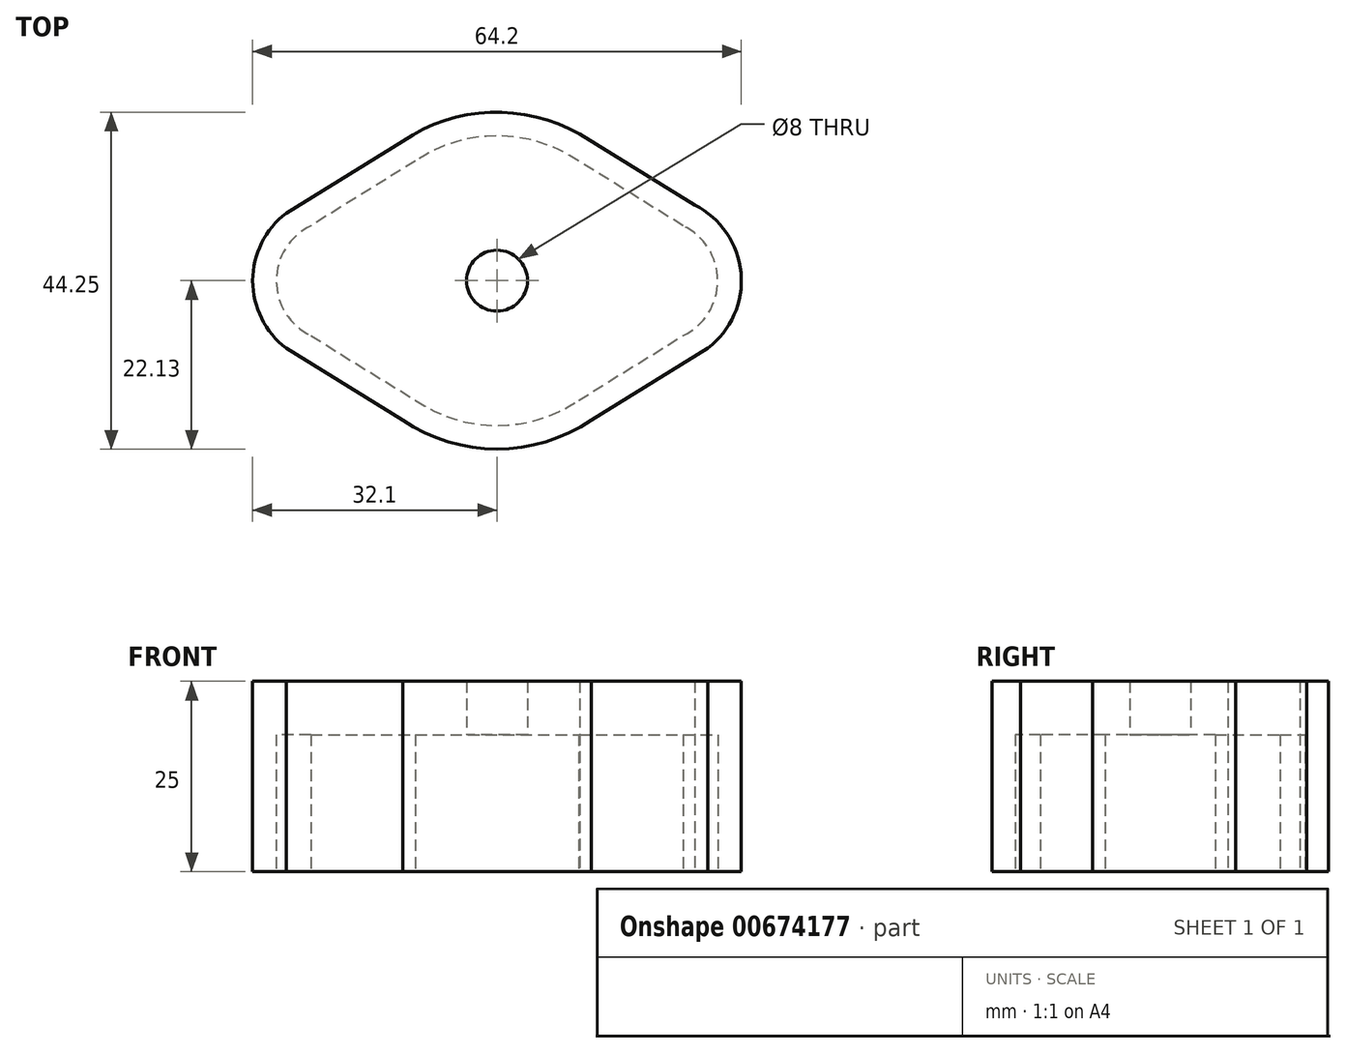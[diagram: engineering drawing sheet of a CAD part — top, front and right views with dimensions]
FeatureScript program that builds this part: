
annotation { "Feature Type Name" : "Feature", "Feature Type Description" : "" }
export const myFeature = defineFeature(function(context is Context, id is Id, definition is map)
    precondition{}
    {
        {
            var Q0;
            Q0=qCreatedBy(makeId("Top.planeOp"),FACE);
            var sketch = newSketch(context, id + "F0", { "sketchPlane" : qUnion([Q0])});
            skPoint(sketch, "E0.middle", {"position": v(0, 0) * mm});
            skArc(sketch, "E1", {"start": v(-12.4, -18.33) * mm, "mid": v(0, -22.12) * mm, "end": v(12.4, -18.33) * mm});
            skLineSegment(sketch, "E2", {"start": v(-27.68, 8.86) * mm, "end": v(-10.88, 19.27) * mm});
            skLineSegment(sketch, "E3", {"start": v(10.88, 19.27) * mm, "end": v(27.68, 8.86) * mm});
            skLineSegment(sketch, "E4", {"start": v(27.68, -8.86) * mm, "end": v(10.88, -19.27) * mm});
            skLineSegment(sketch, "E5", {"start": v(-10.88, -19.27) * mm, "end": v(-27.68, -8.86) * mm});
            skPoint(sketch, "E6.orphan", {"position": v(0, 26) * mm});
            skPoint(sketch, "E7.orphan", {"position": v(0, -26) * mm});
            skArc(sketch, "E8.trimOffspring", {"start": v(12.4, 18.33) * mm, "mid": v(0, 22.12) * mm, "end": v(-12.4, 18.33) * mm});
            skPoint(sketch, "E9.startSnap0", {"position": v(-21, -13) * mm});
            skArc(sketch, "E10", {"start": v(-25.95, 9.93) * mm, "mid": v(-32.1, 0) * mm, "end": v(-25.95, -9.93) * mm});
            skPoint(sketch, "E11.orphan", {"position": v(-42, 0) * mm});
            skArc(sketch, "E12.MirrorC", {"start": v(25.95, 9.93) * mm, "mid": v(32.1, 0) * mm, "end": v(25.95, -9.93) * mm});
            skPoint(sketch, "E13.orphan", {"position": v(42, 0) * mm});
            skPoint(sketch, "E14.start.orphan", {"position": v(-21, -26) * mm});
            skPoint(sketch, "E15.orphan", {"position": v(-42, 26) * mm});
            skPoint(sketch, "E16.orphan", {"position": v(42, 26) * mm});
            skPoint(sketch, "E17.orphan", {"position": v(-42, -26) * mm});
            skPoint(sketch, "E0.top.start.orphan", {"position": v(42, -26) * mm});
            skSolve(sketch);
        }
        {
            var Q0;
            {var subQ0=sQuery(id+"F0.wireOp",EDGE,"E5");var subQ1=sQuery(id+"F0.wireOp",EDGE,"E1");var subQ2=makeQuery(id+"F0.imprint","INTERSECT",VERTEX,{"disambiguationData":[OD(0.0)],"derivedFrom":[subQ1,subQ0]});Q0=makeQuery(id+"F0.imprint","IMPRINT",FACE,{"disambiguationData":[TD([[makeQuery(id+"F0.imprint","IMPRINT",EDGE,{"disambiguationData":[TD([[subQ2,-1.0]])],"derivedFrom":subQ1}),1.0]])]});}
            var Q1;
            {var subQ0=sQuery(id+"F0.wireOp",EDGE,"E4");var subQ1=sQuery(id+"F0.wireOp",EDGE,"E1");var subQ2=makeQuery(id+"F0.imprint","INTERSECT",VERTEX,{"disambiguationData":[OD(0.0)],"derivedFrom":[subQ1,subQ0]});Q1=makeQuery(id+"F0.imprint","IMPRINT",FACE,{"disambiguationData":[TD([[makeQuery(id+"F0.imprint","IMPRINT",EDGE,{"disambiguationData":[TD([[subQ2,1.0]])],"derivedFrom":subQ1}),1.0]])]});}
            var Q2;
            {var subQ0=sQuery(id+"F0.wireOp",EDGE,"E10");var subQ1=sQuery(id+"F0.wireOp",EDGE,"E2");var subQ2=makeQuery(id+"F0.imprint","INTERSECT",VERTEX,{"disambiguationData":[OD(0.0)],"derivedFrom":[subQ1,subQ0]});Q2=makeQuery(id+"F0.imprint","IMPRINT",FACE,{"disambiguationData":[TD([[makeQuery(id+"F0.imprint","IMPRINT",EDGE,{"disambiguationData":[TD([[subQ2,-1.0]])],"derivedFrom":subQ1}),1.0]])]});}
            var Q3;
            {var subQ0=sQuery(id+"F0.wireOp",EDGE,"E8.trimOffspring");var subQ1=sQuery(id+"F0.wireOp",EDGE,"E2");var subQ2=makeQuery(id+"F0.imprint","INTERSECT",VERTEX,{"disambiguationData":[OD(0.0)],"derivedFrom":[subQ1,subQ0]});Q3=makeQuery(id+"F0.imprint","IMPRINT",FACE,{"disambiguationData":[TD([[makeQuery(id+"F0.imprint","IMPRINT",EDGE,{"disambiguationData":[TD([[subQ2,1.0]])],"derivedFrom":subQ1}),1.0]])]});}
            var Q4;
            {var subQ0=sQuery(id+"F0.wireOp",EDGE,"E8.trimOffspring");var subQ1=sQuery(id+"F0.wireOp",EDGE,"E3");var subQ2=makeQuery(id+"F0.imprint","INTERSECT",VERTEX,{"disambiguationData":[OD(0.0)],"derivedFrom":[subQ1,subQ0]});Q4=makeQuery(id+"F0.imprint","IMPRINT",FACE,{"disambiguationData":[TD([[makeQuery(id+"F0.imprint","IMPRINT",EDGE,{"disambiguationData":[TD([[subQ2,-1.0]])],"derivedFrom":subQ1}),1.0]])]});}
            var Q5;
            {var subQ0=sQuery(id+"F0.wireOp",EDGE,"E12.MirrorC");var subQ1=sQuery(id+"F0.wireOp",EDGE,"E3");var subQ2=makeQuery(id+"F0.imprint","INTERSECT",VERTEX,{"disambiguationData":[OD(0.0)],"derivedFrom":[subQ1,subQ0]});Q5=makeQuery(id+"F0.imprint","IMPRINT",FACE,{"disambiguationData":[TD([[makeQuery(id+"F0.imprint","IMPRINT",EDGE,{"disambiguationData":[TD([[subQ2,1.0]])],"derivedFrom":subQ1}),1.0]])]});}
            var Q6;
            {var subQ0=sQuery(id+"F0.wireOp",EDGE,"E12.MirrorC");var subQ1=sQuery(id+"F0.wireOp",EDGE,"E4");var subQ2=makeQuery(id+"F0.imprint","INTERSECT",VERTEX,{"disambiguationData":[OD(0.0)],"derivedFrom":[subQ1,subQ0]});Q6=makeQuery(id+"F0.imprint","IMPRINT",FACE,{"disambiguationData":[TD([[makeQuery(id+"F0.imprint","IMPRINT",EDGE,{"disambiguationData":[TD([[subQ2,-1.0]])],"derivedFrom":subQ1}),1.0]])]});}
            var Q7;
            {var subQ0=sQuery(id+"F0.wireOp",EDGE,"E10");var subQ1=sQuery(id+"F0.wireOp",EDGE,"E5");var subQ2=makeQuery(id+"F0.imprint","INTERSECT",VERTEX,{"disambiguationData":[OD(0.0)],"derivedFrom":[subQ1,subQ0]});Q7=makeQuery(id+"F0.imprint","IMPRINT",FACE,{"disambiguationData":[TD([[makeQuery(id+"F0.imprint","IMPRINT",EDGE,{"disambiguationData":[TD([[subQ2,1.0]])],"derivedFrom":subQ1}),1.0]])]});}
            var Q8;
            {var subQ0=sQuery(id+"F0.wireOp",EDGE,"E4");var subQ1=sQuery(id+"F0.wireOp",EDGE,"E1");var subQ3=makeQuery(id+"F0.imprint","INTERSECT",VERTEX,{"disambiguationData":[OD(1.0)],"derivedFrom":[subQ1,subQ0]});Q8=makeQuery(id+"F0.imprint","IMPRINT",FACE,{"disambiguationData":[TD([[makeQuery(id+"F0.imprint","IMPRINT",EDGE,{"disambiguationData":[TD([[subQ3,1.0]])],"derivedFrom":subQ1}),1.0]])]});}
            extrude(context, id + "F1", {"entities" : qUnion([Q0, Q1, Q2, Q3, Q4, Q5, Q6, Q7, Q8]), "depth" : 25 * mm, "offsetDistance" : 25 * mm});
        }
        {
            var Q0;
            Q0=qCreatedBy(makeId("Top.planeOp"),FACE);
            var sketch = newSketch(context, id + "F2", { "sketchPlane" : qUnion([Q0])});
            skLineSegment(sketch, "E18.0", {"start": v(-24.45, -7.22) * mm, "end": v(-10.7, -15.72) * mm});
            skArc(sketch, "E18.1", {"start": v(-24.45, 7.22) * mm, "mid": v(-29, 0) * mm, "end": v(-24.45, -7.22) * mm});
            skArc(sketch, "E18.2", {"start": v(-10.7, -15.72) * mm, "mid": v(0, -19.02) * mm, "end": v(10.7, -15.72) * mm});
            skLineSegment(sketch, "E18.3", {"start": v(-10.7, 15.72) * mm, "end": v(-24.45, 7.22) * mm});
            skLineSegment(sketch, "E18.4", {"start": v(10.7, -15.72) * mm, "end": v(24.45, -7.22) * mm});
            skArc(sketch, "E18.5", {"start": v(24.45, -7.22) * mm, "mid": v(29, 0) * mm, "end": v(24.45, 7.22) * mm});
            skLineSegment(sketch, "E18.6", {"start": v(24.45, 7.22) * mm, "end": v(10.7, 15.72) * mm});
            skArc(sketch, "E18.7", {"start": v(10.7, 15.72) * mm, "mid": v(0, 19.02) * mm, "end": v(-10.7, 15.72) * mm});
            skSolve(sketch);
        }
        {
            var Q0;
            Q0=makeQuery(id+"F2.imprint","IMPRINT",FACE,{"disambiguationData":[TD([[makeQuery(id+"F2.imprint","IMPRINT",EDGE,{"derivedFrom":sQuery(id+"F2.wireOp",EDGE,"E18.0")}),1.0]])]});
            extrude(context, id + "F3", {"entities" : qUnion([Q0]), "operationType" : NewBodyOperationType.REMOVE, "depth" : 18 * mm, "offsetDistance" : 25 * mm});
        }
        {
            var Q0;
            Q0=qCreatedBy(makeId("Top.planeOp"),FACE);
            var sketch = newSketch(context, id + "F4", { "sketchPlane" : qUnion([Q0])});
            skCircle(sketch, "E19", {"center": v(0, 0) * mm, "radius": 4 * mm});
            skSolve(sketch);
        }
        {
            var Q0;
            Q0 = qSketchRegion(id + "F4", true);
            extrude(context, id + "F5", {"entities" : qUnion([Q0]), "operationType" : NewBodyOperationType.REMOVE, "endBound" : BoundingType.THROUGH_ALL, "depth" : 25 * mm, "offsetDistance" : 25 * mm});
        }
    });
